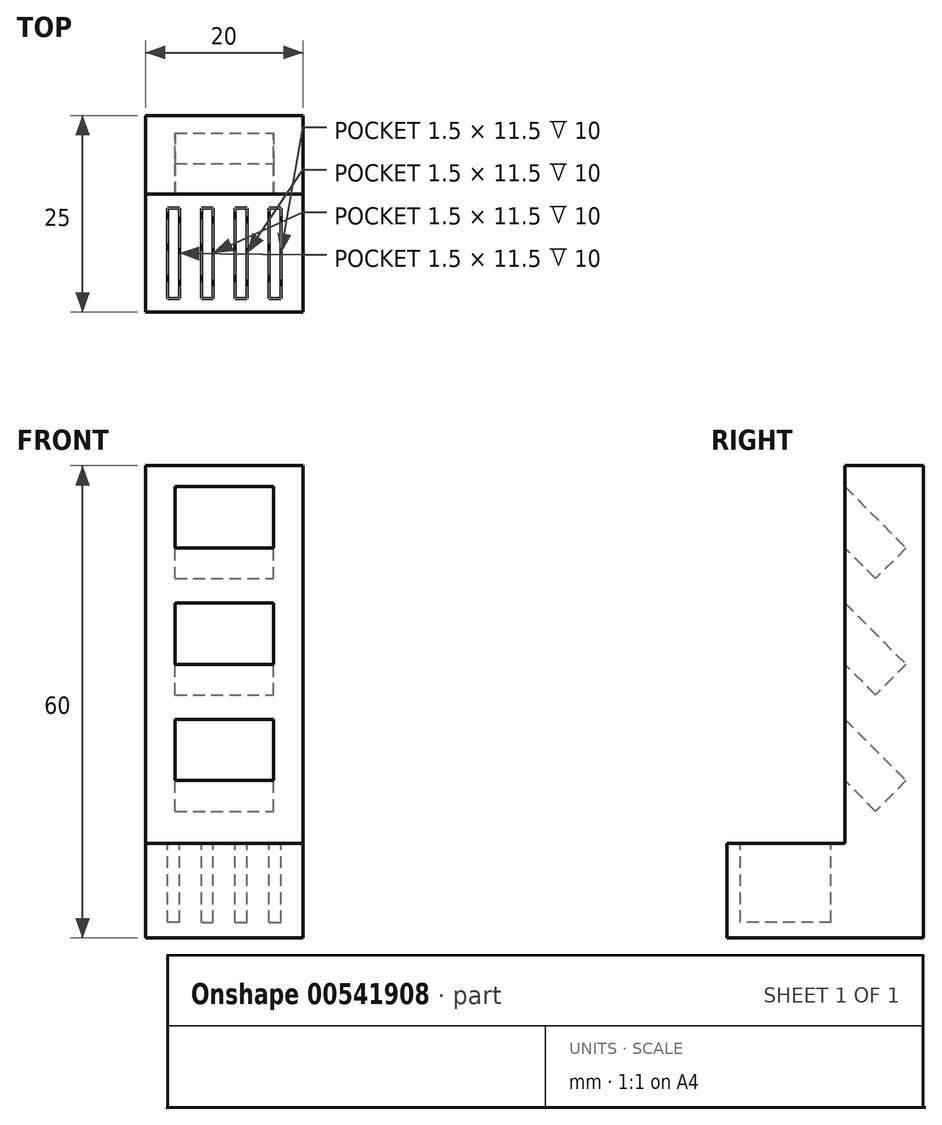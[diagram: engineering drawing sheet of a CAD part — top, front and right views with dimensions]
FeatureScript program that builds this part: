
annotation { "Feature Type Name" : "Feature", "Feature Type Description" : "" }
export const myFeature = defineFeature(function(context is Context, id is Id, definition is map)
    precondition{}
    {
        {
            var Q0;
            Q0=qCreatedBy(makeId("Right.planeOp"),FACE);
            var sketch = newSketch(context, id + "F0", { "sketchPlane" : qUnion([Q0])});
            skLineSegment(sketch, "E0.bottom", {"start": v(0, 0) * mm, "end": v(-25, 0) * mm});
            skLineSegment(sketch, "E0.top", {"start": v(-10, 12) * mm, "end": v(-25, 12) * mm});
            skLineSegment(sketch, "E0.right", {"start": v(-25, 0) * mm, "end": v(-25, 12) * mm});
            skLineSegment(sketch, "E1.top", {"start": v(0, 60) * mm, "end": v(-10, 60) * mm});
            skLineSegment(sketch, "E1.left", {"start": v(0, 0) * mm, "end": v(0, 60) * mm});
            skLineSegment(sketch, "E1.right", {"start": v(-10, 12) * mm, "end": v(-10, 60) * mm});
            skSolve(sketch);
        }
        {
            var Q0;
            Q0 = qSketchRegion(id + "F0", true);
            extrude(context, id + "F1", {"entities" : qUnion([Q0]), "endBound" : BoundingType.SYMMETRIC, "depth" : 20 * mm, "offsetDistance" : 25.4 * mm});
        }
        {
            var Q0;
            Q0=qCreatedBy(makeId("Right.planeOp"),FACE);
            var sketch = newSketch(context, id + "F2", { "sketchPlane" : qUnion([Q0])});
            skLineSegment(sketch, "E2.0.0", {"start": v(-10, 12) * mm, "end": v(-10, 60) * mm, "construction": true});
            skLineSegment(sketch, "E2.0.1", {"start": v(-10, 60) * mm, "end": v(0, 60) * mm, "construction": true});
            skLineSegment(sketch, "E2.0.2", {"start": v(0, 60) * mm, "end": v(0, 0) * mm, "construction": true});
            skLineSegment(sketch, "E2.0.3", {"start": v(0, 0) * mm, "end": v(-25, 0) * mm, "construction": true});
            skLineSegment(sketch, "E2.0.4", {"start": v(-25, 0) * mm, "end": v(-25, 12) * mm, "construction": true});
            skLineSegment(sketch, "E2.0.5", {"start": v(-25, 12) * mm, "end": v(-10, 12) * mm, "construction": true});
            skLineSegment(sketch, "E3", {"start": v(-10, 57.33) * mm, "end": v(-2.22, 49.56) * mm});
            skLineSegment(sketch, "E4", {"start": v(-2.22, 49.56) * mm, "end": v(-6.11, 45.67) * mm});
            skLineSegment(sketch, "E5", {"start": v(-6.11, 45.67) * mm, "end": v(-10, 49.56) * mm});
            skLineSegment(sketch, "E6", {"start": v(-10, 57.33) * mm, "end": v(-10, 49.56) * mm});
            skLineSegment(sketch, "E7", {"start": v(-10, 42.56) * mm, "end": v(-2.22, 34.78) * mm});
            skLineSegment(sketch, "E8", {"start": v(-2.22, 34.78) * mm, "end": v(-6.11, 30.89) * mm});
            skLineSegment(sketch, "E9", {"start": v(-6.11, 30.89) * mm, "end": v(-10, 34.78) * mm});
            skLineSegment(sketch, "E10", {"start": v(-10, 34.78) * mm, "end": v(-10, 42.56) * mm});
            skLineSegment(sketch, "E11", {"start": v(-10, 27.78) * mm, "end": v(-2.22, 20) * mm});
            skLineSegment(sketch, "E12", {"start": v(-2.22, 20) * mm, "end": v(-6.11, 16.11) * mm});
            skLineSegment(sketch, "E13", {"start": v(-6.11, 16.11) * mm, "end": v(-10, 20) * mm});
            skLineSegment(sketch, "E14", {"start": v(-10, 20) * mm, "end": v(-10, 27.78) * mm});
            skSolve(sketch);
        }
        {
            var Q0;
            Q0 = qSketchRegion(id + "F2", true);
            extrude(context, id + "F3", {"entities" : qUnion([Q0]), "operationType" : NewBodyOperationType.REMOVE, "endBound" : BoundingType.SYMMETRIC, "oppositeDirection" : true, "depth" : 12.5 * mm, "offsetDistance" : 25.4 * mm});
        }
        {
            var Q0;
            Q0=makeQuery(id+"F1.opExtrude","SWEPT_FACE",FACE,{"disambiguationData":[OSD([sQuery(id+"F0.wireOp",EDGE,"E0.top")])]});
            var sketch = newSketch(context, id + "F4", { "sketchPlane" : qUnion([Q0])});
            skLineSegment(sketch, "E15", {"start": v(-10, -17.5) * mm, "end": v(10, -17.5) * mm, "construction": true});
            skLineSegment(sketch, "E16.bottom", {"start": v(-5.7, -11.75) * mm, "end": v(-7.2, -11.75) * mm});
            skLineSegment(sketch, "E16.top", {"start": v(-5.7, -23.25) * mm, "end": v(-7.2, -23.25) * mm});
            skLineSegment(sketch, "E16.left", {"start": v(-5.7, -11.75) * mm, "end": v(-5.7, -23.25) * mm});
            skLineSegment(sketch, "E16.right", {"start": v(-7.2, -11.75) * mm, "end": v(-7.2, -23.25) * mm});
            skPoint(sketch, "E16.middle", {"position": v(-6.45, -17.5) * mm});
            skLineSegment(sketch, "E17.bottom", {"start": v(-2.9, -11.75) * mm, "end": v(-1.4, -11.75) * mm});
            skLineSegment(sketch, "E17.top", {"start": v(-2.9, -23.25) * mm, "end": v(-1.4, -23.25) * mm});
            skLineSegment(sketch, "E17.left", {"start": v(-2.9, -11.75) * mm, "end": v(-2.9, -23.25) * mm});
            skLineSegment(sketch, "E17.right", {"start": v(-1.4, -11.75) * mm, "end": v(-1.4, -23.25) * mm});
            skPoint(sketch, "E17.middle", {"position": v(-2.15, -17.5) * mm});
            skLineSegment(sketch, "E18.bottom", {"start": v(1.4, -11.75) * mm, "end": v(2.9, -11.75) * mm});
            skLineSegment(sketch, "E18.top", {"start": v(1.4, -23.25) * mm, "end": v(2.9, -23.25) * mm});
            skLineSegment(sketch, "E18.left", {"start": v(1.4, -11.75) * mm, "end": v(1.4, -23.25) * mm});
            skLineSegment(sketch, "E18.right", {"start": v(2.9, -11.75) * mm, "end": v(2.9, -23.25) * mm});
            skPoint(sketch, "E18.middle", {"position": v(2.15, -17.5) * mm});
            skLineSegment(sketch, "E19.bottom", {"start": v(5.7, -11.75) * mm, "end": v(7.2, -11.75) * mm});
            skLineSegment(sketch, "E19.top", {"start": v(5.7, -23.25) * mm, "end": v(7.2, -23.25) * mm});
            skLineSegment(sketch, "E19.left", {"start": v(5.7, -11.75) * mm, "end": v(5.7, -23.25) * mm});
            skLineSegment(sketch, "E19.right", {"start": v(7.2, -11.75) * mm, "end": v(7.2, -23.25) * mm});
            skPoint(sketch, "E19.middle", {"position": v(6.45, -17.5) * mm});
            skLineSegment(sketch, "E20", {"start": v(-7.2, -11.75) * mm, "end": v(-10, -11.75) * mm, "construction": true});
            skLineSegment(sketch, "E21", {"start": v(-5.7, -11.75) * mm, "end": v(-2.9, -11.75) * mm, "construction": true});
            skLineSegment(sketch, "E22", {"start": v(-1.4, -11.75) * mm, "end": v(1.4, -11.75) * mm, "construction": true});
            skLineSegment(sketch, "E23", {"start": v(2.9, -11.75) * mm, "end": v(5.7, -11.75) * mm, "construction": true});
            skLineSegment(sketch, "E24", {"start": v(7.2, -11.75) * mm, "end": v(10, -11.75) * mm, "construction": true});
            skSolve(sketch);
        }
        {
            var Q0;
            Q0 = qSketchRegion(id + "F4", true);
            extrude(context, id + "F5", {"entities" : qUnion([Q0]), "operationType" : NewBodyOperationType.REMOVE, "oppositeDirection" : true, "depth" : 10 * mm, "offsetDistance" : 25.4 * mm});
        }
    });
